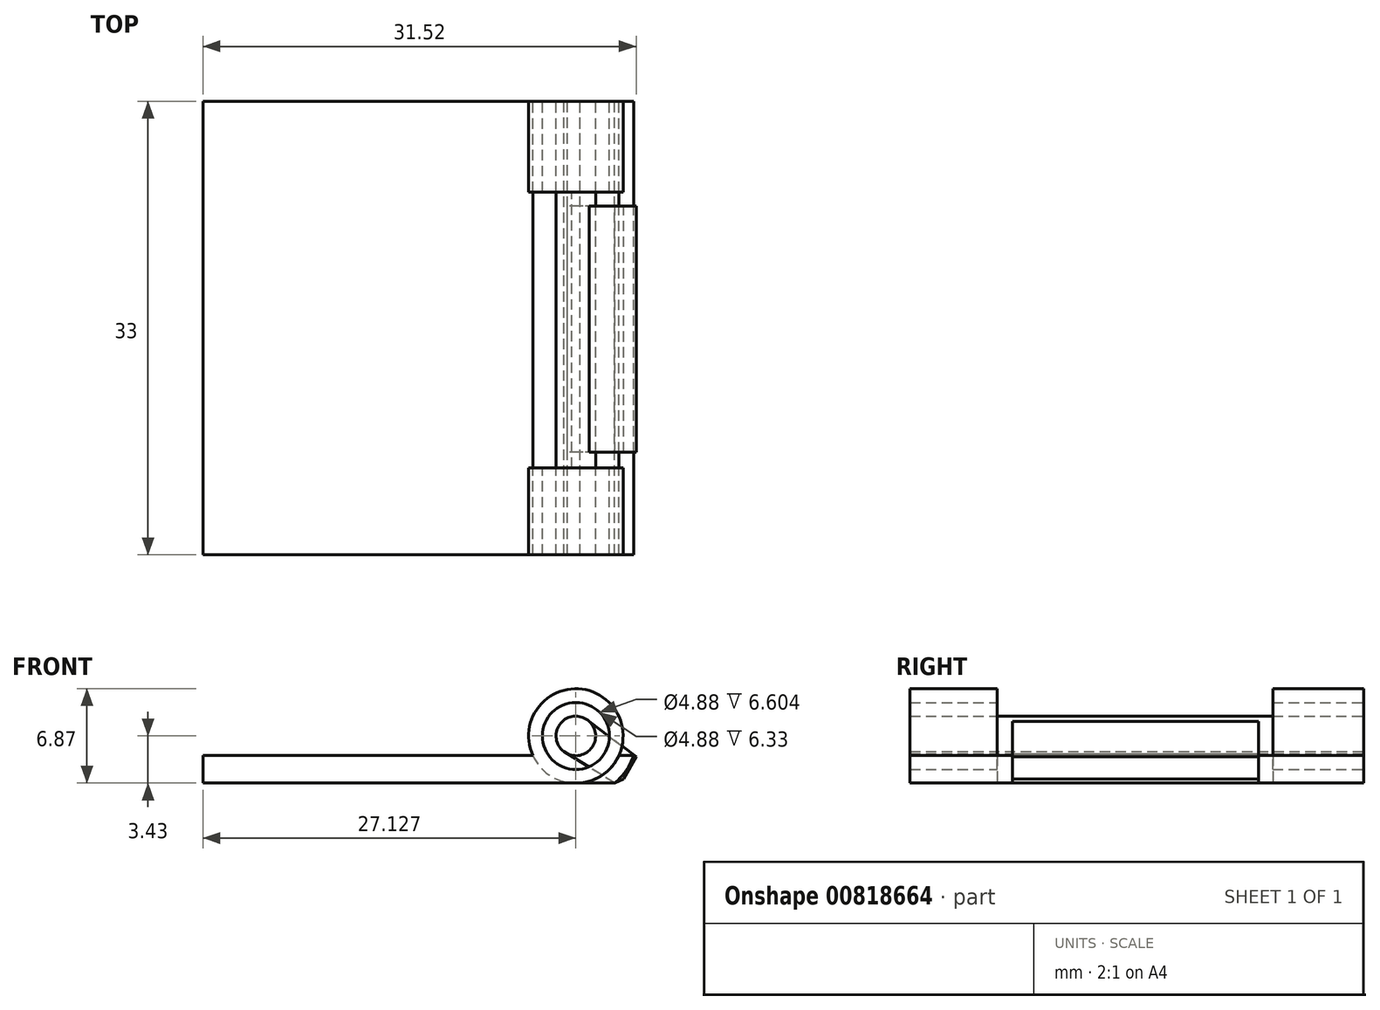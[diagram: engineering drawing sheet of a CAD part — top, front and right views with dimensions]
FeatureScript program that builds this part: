
annotation { "Feature Type Name" : "Feature", "Feature Type Description" : "" }
export const myFeature = defineFeature(function(context is Context, id is Id, definition is map)
    precondition{}
    {
        {
            var Q0;
            Q0=qCreatedBy(makeId("Front.planeOp"),FACE);
            var sketch = newSketch(context, id + "F0", { "sketchPlane" : qUnion([Q0])});
            skLineSegment(sketch, "E0.bottom", {"start": v(-25.91, 16.7) * mm, "end": v(-1.91, 16.7) * mm});
            skLineSegment(sketch, "E0.top", {"start": v(-25.91, 14.7) * mm, "end": v(-1.91, 14.7) * mm});
            skLineSegment(sketch, "E0.left", {"start": v(-25.91, 16.7) * mm, "end": v(-25.91, 14.7) * mm});
            skLineSegment(sketch, "E0.right", {"start": v(-1.91, 16.7) * mm, "end": v(-1.91, 14.7) * mm});
            skLineSegment(sketch, "E1", {"start": v(-1.91, 14.7) * mm, "end": v(3.38, 14.7) * mm});
            skCircle(sketch, "E2", {"center": v(1.22, 18.12) * mm, "radius": 3.44 * mm});
            skCircle(sketch, "E3", {"center": v(1.22, 18.12) * mm, "radius": 2.44 * mm});
            skSolve(sketch);
        }
        {
            var Q0;
            Q0=makeQuery(id+"F0.imprint","IMPRINT",FACE,{"disambiguationData":[TD([[makeQuery(id+"F0.imprint","IMPRINT",EDGE,{"derivedFrom":sQuery(id+"F0.wireOp",EDGE,"E0.bottom")}),-1.0]])]});
            var Q1;
            {var subQ0=sQuery(id+"F0.wireOp",EDGE,"E0.right");Q1=makeQuery(id+"F0.imprint","IMPRINT",FACE,{"disambiguationData":[TD([[makeQuery(id+"F0.imprint","IMPRINT",EDGE,{"derivedFrom":subQ0}),1.0]])]});}
            extrude(context, id + "F1", {"entities" : qUnion([Q0, Q1]), "depth" : 33 * mm, "offsetDistance" : 25.4 * mm});
        }
        {
            var Q0;
            Q0=makeQuery(id+"F0.imprint","IMPRINT",FACE,{"disambiguationData":[TD([[makeQuery(id+"F0.imprint","IMPRINT",EDGE,{"derivedFrom":sQuery(id+"F0.wireOp",EDGE,"E3")}),-1.0]])]});
            extrude(context, id + "F2", {"entities" : qUnion([Q0]), "operationType" : NewBodyOperationType.ADD, "depth" : 6.6 * mm, "offsetDistance" : 25.4 * mm});
        }
        {
            var Q0;
            Q0=makeQuery(id+"F0.imprint","IMPRINT",FACE,{"disambiguationData":[TD([[makeQuery(id+"F0.imprint","IMPRINT",EDGE,{"derivedFrom":sQuery(id+"F0.wireOp",EDGE,"E3")}),-1.0]])]});
            var Q1;
            Q1=makeQuery(id+"F1.opExtrude","CAP_FACE",FACE,{"disambiguationData":[OSD([sQuery(id+"F0.wireOp",EDGE,"E0.bottom"),sQuery(id+"F0.wireOp",EDGE,"E0.top"),sQuery(id+"F0.wireOp",EDGE,"E0.left"),sQuery(id+"F0.wireOp",EDGE,"E1"),sQuery(id+"F0.wireOp",EDGE,"E2")])],"isStart":false});
            extrude(context, id + "F3", {"entities" : qUnion([Q0]), "operationType" : NewBodyOperationType.ADD, "endBound" : BoundingType.UP_TO_SURFACE, "depth" : 25.4 * mm, "endBoundEntityFace" : qUnion([Q1]), "offsetDistance" : 25.4 * mm, "hasSecondDirection" : true, "secondDirectionOppositeDirection" : false, "secondDirectionDepth" : 26.67 * mm});
        }
        {
            var Q0;
            {var subQ0=sQuery(id+"F0.wireOp",EDGE,"E2");var subQ1=sQuery(id+"F0.wireOp",EDGE,"E1");Q0=makeQuery(id+"F2.boolean.opBoolean","MERGE",FACE,{"derivedFrom":[makeQuery(id+"F1.opExtrude","CAP_FACE",FACE,{"disambiguationData":[OSD([sQuery(id+"F0.wireOp",EDGE,"E0.bottom"),sQuery(id+"F0.wireOp",EDGE,"E0.top"),sQuery(id+"F0.wireOp",EDGE,"E0.left"),subQ1,subQ0])],"isStart":true}),makeQuery(id+"F2.opExtrude","CAP_FACE",FACE,{"disambiguationData":[OSD([subQ1,subQ0,sQuery(id+"F0.wireOp",EDGE,"E3")])],"isStart":true})]});}
            var sketch = newSketch(context, id + "F4", { "sketchPlane" : qUnion([Q0])});
            skArc(sketch, "E4.0", {"start": v(-4.04, 14.7) * mm, "mid": v(-4.87, 15.6) * mm, "end": v(-5.42, 16.7) * mm});
            skLineSegment(sketch, "E5", {"start": v(1.91, 16.7) * mm, "end": v(-10.07, 16.7) * mm});
            skLineSegment(sketch, "E6", {"start": v(-1.5, 14.7) * mm, "end": v(-15.85, 14.7) * mm});
            skLineSegment(sketch, "E7", {"start": v(-4.04, 14.7) * mm, "end": v(-28.04, 14.7) * mm});
            skLineSegment(sketch, "E8", {"start": v(-28.04, 14.7) * mm, "end": v(-28.04, 16.7) * mm});
            skLineSegment(sketch, "E9", {"start": v(-28.04, 16.7) * mm, "end": v(-10.07, 16.7) * mm});
            skSolve(sketch);
        }
        {
            var Q0;
            {var subQ2=sQuery(id+"F4.wireOp",EDGE,"E4.0");Q0=makeQuery(id+"F4.imprint","IMPRINT",FACE,{"disambiguationData":[TD([[makeQuery(id+"F4.imprint","IMPRINT",EDGE,{"derivedFrom":subQ2}),1.0]])]});}
            var Q1;
            {var subQ0=sQuery(id+"F0.wireOp",EDGE,"E2");var subQ1=sQuery(id+"F0.wireOp",EDGE,"E1");var subQ2=sQuery(id+"F0.wireOp",EDGE,"E0.left");var subQ3=sQuery(id+"F0.wireOp",EDGE,"E0.top");var subQ4=sQuery(id+"F0.wireOp",EDGE,"E0.bottom");Q1=makeQuery(id+"F3.boolean.opBoolean","MERGE",FACE,{"derivedFrom":[makeQuery(id+"F1.opExtrude","CAP_FACE",FACE,{"disambiguationData":[OSD([subQ4,subQ3,subQ2,subQ1,subQ0])],"isStart":false}),makeQuery(id+"F3.opExtrude","CAP_FACE",FACE,{"disambiguationData":[OSD([subQ4,subQ3,subQ2,subQ1,subQ0])],"isStart":false})]});}
            extrude(context, id + "F5", {"entities" : qUnion([Q0]), "endBound" : BoundingType.UP_TO_SURFACE, "oppositeDirection" : true, "depth" : 32.56 * mm, "endBoundEntityFace" : qUnion([Q1]), "offsetDistance" : 25.4 * mm});
        }
        {
            var Q0;
            {var subQ0=sQuery(id+"F0.wireOp",EDGE,"E2");var subQ1=sQuery(id+"F0.wireOp",EDGE,"E1");Q0=makeQuery(id+"F2.boolean.opBoolean","MERGE",FACE,{"derivedFrom":[makeQuery(id+"F1.opExtrude","CAP_FACE",FACE,{"disambiguationData":[OSD([sQuery(id+"F0.wireOp",EDGE,"E0.bottom"),sQuery(id+"F0.wireOp",EDGE,"E0.top"),sQuery(id+"F0.wireOp",EDGE,"E0.left"),subQ1,subQ0])],"isStart":true}),makeQuery(id+"F2.opExtrude","CAP_FACE",FACE,{"disambiguationData":[OSD([subQ1,subQ0,sQuery(id+"F0.wireOp",EDGE,"E3")])],"isStart":true})]});}
            var sketch = newSketch(context, id + "F6", { "sketchPlane" : qUnion([Q0])});
            skCircle(sketch, "E10.0", {"center": v(-1.22, 18.12) * mm, "radius": 1.44 * mm});
            skLineSegment(sketch, "E11", {"start": v(-2.2, 19.18) * mm, "end": v(-5.61, 16.6) * mm});
            skLineSegment(sketch, "E12", {"start": v(-5.61, 16.6) * mm, "end": v(-4.68, 15) * mm});
            skLineSegment(sketch, "E13", {"start": v(-4.68, 15) * mm, "end": v(-4.05, 14.7) * mm});
            skLineSegment(sketch, "E14", {"start": v(-4.05, 14.7) * mm, "end": v(-0.34, 16.98) * mm});
            skSolve(sketch);
        }
        {
            var Q0;
            {var subQ0=sQuery(id+"F6.wireOp",EDGE,"E10.0");var subQ1=makeQuery(id+"F6.imprint","INTERSECT",VERTEX,{"derivedFrom":[subQ0,sQuery(id+"F6.wireOp",EDGE,"E11")]});Q0=makeQuery(id+"F6.imprint","IMPRINT",FACE,{"disambiguationData":[TD([[makeQuery(id+"F6.imprint","IMPRINT",EDGE,{"disambiguationData":[TD([[subQ1,-1.0]])],"derivedFrom":subQ0}),1.0]])]});}
            var Q1;
            {var subQ0=sQuery(id+"F0.wireOp",EDGE,"E2");var subQ1=sQuery(id+"F0.wireOp",EDGE,"E1");var subQ2=sQuery(id+"F0.wireOp",EDGE,"E0.left");var subQ3=sQuery(id+"F0.wireOp",EDGE,"E0.top");var subQ4=sQuery(id+"F0.wireOp",EDGE,"E0.bottom");Q1=makeQuery(id+"F3.boolean.opBoolean","MERGE",FACE,{"derivedFrom":[makeQuery(id+"F1.opExtrude","CAP_FACE",FACE,{"disambiguationData":[OSD([subQ4,subQ3,subQ2,subQ1,subQ0])],"isStart":false}),makeQuery(id+"F3.opExtrude","CAP_FACE",FACE,{"disambiguationData":[OSD([subQ4,subQ3,subQ2,subQ1,subQ0])],"isStart":false})]});}
            extrude(context, id + "F7", {"entities" : qUnion([Q0]), "endBound" : BoundingType.UP_TO_SURFACE, "oppositeDirection" : true, "depth" : 17.32 * mm, "endBoundEntityFace" : qUnion([Q1]), "offsetDistance" : 25.4 * mm});
        }
        {
            var Q0;
            {var subQ4=sQuery(id+"F6.wireOp",EDGE,"E12");Q0=makeQuery(id+"F6.imprint","IMPRINT",FACE,{"disambiguationData":[TD([[makeQuery(id+"F6.imprint","IMPRINT",EDGE,{"derivedFrom":subQ4}),1.0]])]});}
            var Q1;
            {var subQ0=sQuery(id+"F6.wireOp",EDGE,"E11");var subQ1=sQuery(id+"F6.wireOp",EDGE,"E10.0");var subQ2=makeQuery(id+"F6.imprint","INTERSECT",VERTEX,{"derivedFrom":[subQ1,subQ0]});Q1=makeQuery(id+"F6.imprint","IMPRINT",FACE,{"disambiguationData":[TD([[makeQuery(id+"F6.imprint","IMPRINT",EDGE,{"disambiguationData":[TD([[subQ2,-1.0]])],"derivedFrom":subQ1}),-1.0]])]});}
            var Q2;
            {var subQ0=sQuery(id+"F6.wireOp",EDGE,"E11");var subQ1=makeQuery(id+"F2.opExtrude","CAP_EDGE",EDGE,{"disambiguationData":[OSD([sQuery(id+"F0.wireOp",EDGE,"E2")])],"isStart":true});var subQ2=makeQuery(id+"F6.imprint","INTERSECT",VERTEX,{"derivedFrom":[subQ1,subQ0]});Q2=makeQuery(id+"F6.imprint","IMPRINT",FACE,{"disambiguationData":[TD([[makeQuery(id+"F6.imprint","IMPRINT",EDGE,{"disambiguationData":[TD([[subQ2,1.0]])],"derivedFrom":subQ0}),1.0]])]});}
            extrude(context, id + "F8", {"entities" : qUnion([Q0, Q1, Q2]), "oppositeDirection" : true, "depth" : 25.55 * mm, "offsetDistance" : 25.4 * mm, "hasSecondDirection" : true, "secondDirectionOppositeDirection" : true, "secondDirectionDepth" : 7.65 * mm});
        }
    });
